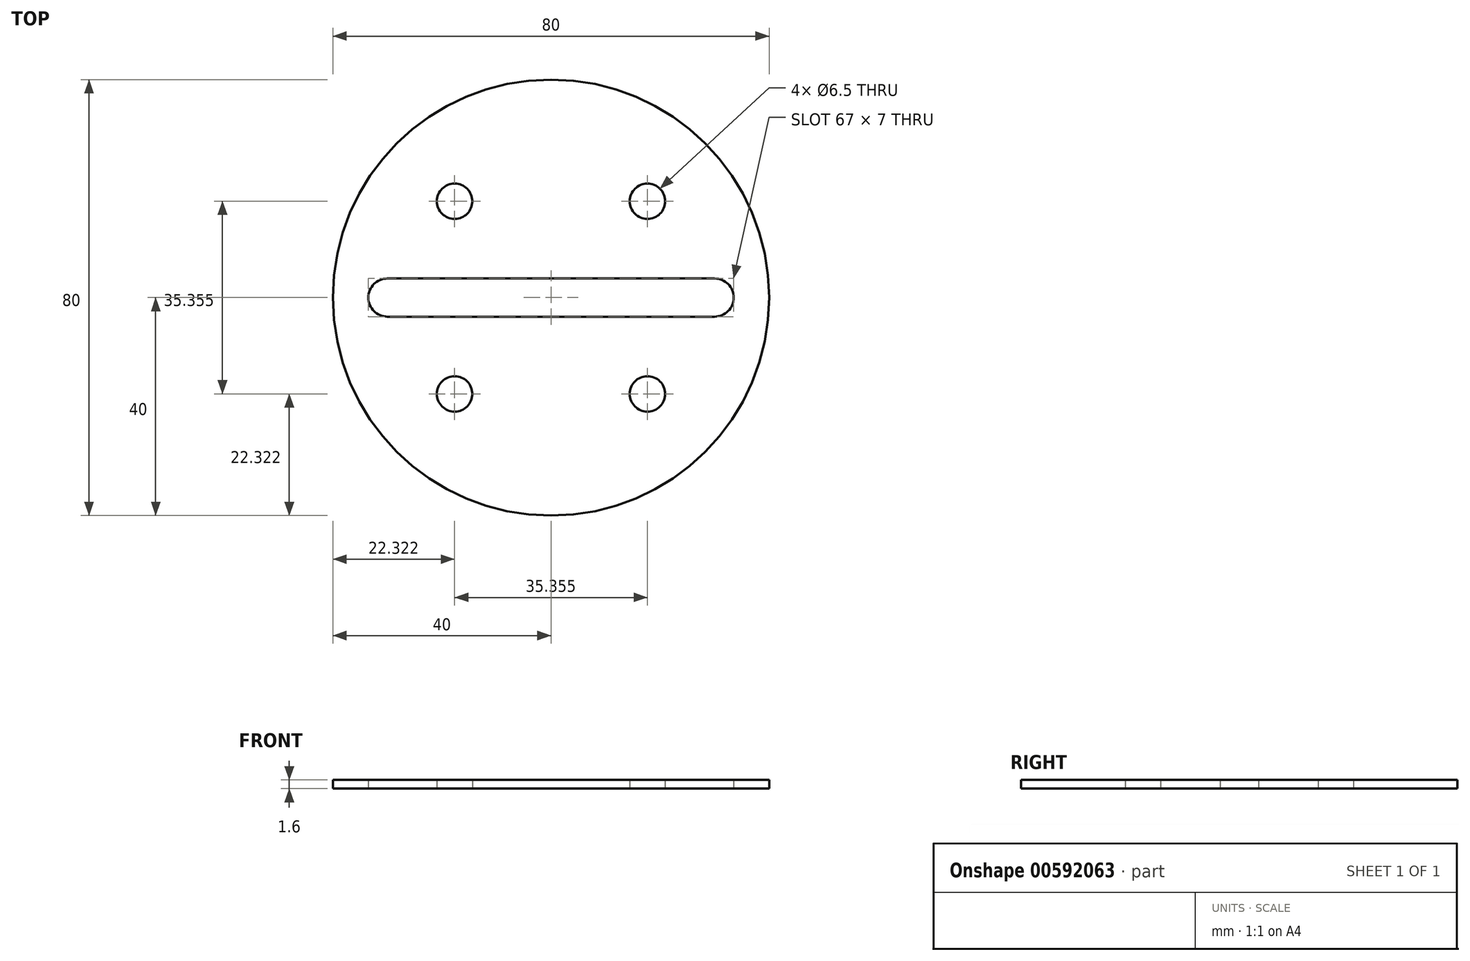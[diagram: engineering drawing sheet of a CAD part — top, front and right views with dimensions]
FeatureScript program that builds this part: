
annotation { "Feature Type Name" : "Feature", "Feature Type Description" : "" }
export const myFeature = defineFeature(function(context is Context, id is Id, definition is map)
    precondition{}
    {
        {
            var Q0;
            Q0=qCreatedBy(makeId("Top.planeOp"),FACE);
            var sketch = newSketch(context, id + "F0", { "sketchPlane" : qUnion([Q0])});
            skCircle(sketch, "E0", {"center": v(0, 0) * mm, "radius": 40 * mm});
            skCircle(sketch, "E1", {"center": v(17.68, 17.68) * mm, "radius": 3.25 * mm});
            skCircle(sketch, "E2.MirrorC", {"center": v(17.68, -17.68) * mm, "radius": 3.25 * mm});
            skCircle(sketch, "E3.MirrorC", {"center": v(-17.68, -17.68) * mm, "radius": 3.25 * mm});
            skCircle(sketch, "E4.MirrorC", {"center": v(-17.68, 17.68) * mm, "radius": 3.25 * mm});
            skLineSegment(sketch, "E5", {"start": v(0, 0) * mm, "end": v(17.68, 17.68) * mm, "construction": true});
            skLineSegment(sketch, "E6.bottom", {"start": v(-30, 3.5) * mm, "end": v(30, 3.5) * mm});
            skLineSegment(sketch, "E6.top", {"start": v(-30, -3.5) * mm, "end": v(30, -3.5) * mm});
            skLineSegment(sketch, "E6.left", {"start": v(-30, 3.5) * mm, "end": v(-30, -3.5) * mm, "construction": true});
            skLineSegment(sketch, "E6.right", {"start": v(30, 3.5) * mm, "end": v(30, -3.5) * mm, "construction": true});
            skArc(sketch, "E7", {"start": v(-30, 3.5) * mm, "mid": v(-33.5, 0) * mm, "end": v(-30, -3.5) * mm});
            skArc(sketch, "E8", {"start": v(30, -3.5) * mm, "mid": v(33.5, 0) * mm, "end": v(30, 3.5) * mm});
            skSolve(sketch);
        }
        {
            var Q0;
            Q0=makeQuery(id+"F0.imprint","IMPRINT",FACE,{"disambiguationData":[TD([[makeQuery(id+"F0.imprint","IMPRINT",EDGE,{"derivedFrom":sQuery(id+"F0.wireOp",EDGE,"E0")}),1.0]])]});
            extrude(context, id + "F1", {"entities" : qUnion([Q0]), "depth" : 1.6 * mm, "offsetDistance" : 25 * mm});
        }
    });
